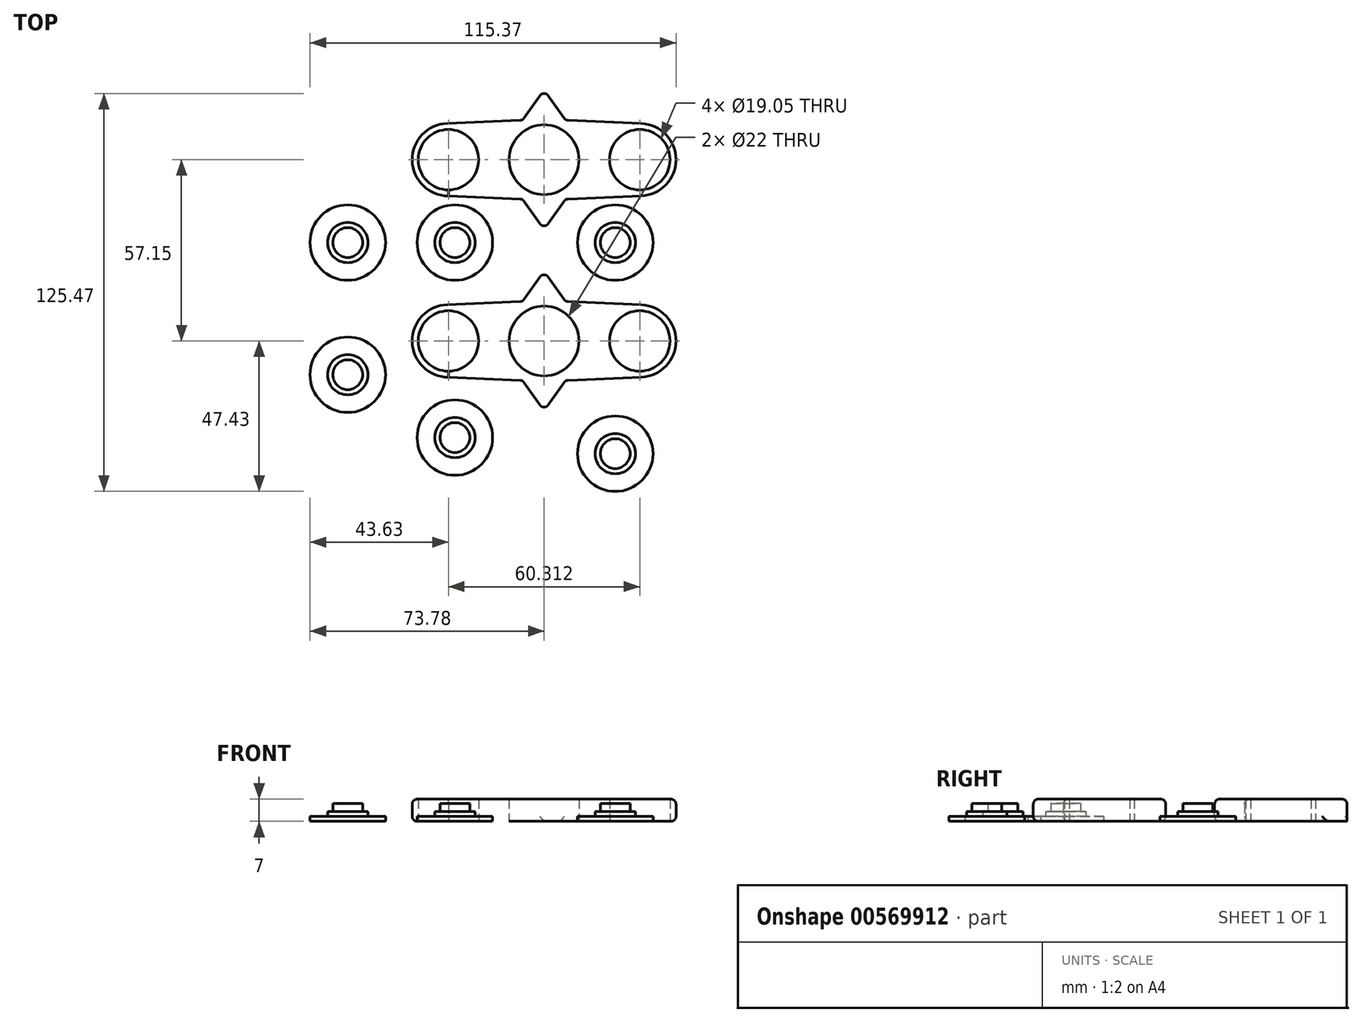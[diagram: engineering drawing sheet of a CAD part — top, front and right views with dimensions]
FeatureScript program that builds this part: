
annotation { "Feature Type Name" : "Feature", "Feature Type Description" : "" }
export const myFeature = defineFeature(function(context is Context, id is Id, definition is map)
    precondition{}
    {
        {
            var Q0;
            Q0=qCreatedBy(makeId("Top.planeOp"),FACE);
            var sketch = newSketch(context, id + "F0", { "sketchPlane" : qUnion([Q0])});
            skCircle(sketch, "E0", {"center": v(0, 0) * mm, "radius": 11 * mm});
            skCircle(sketch, "E1", {"center": v(-30.15, 0) * mm, "radius": 9.53 * mm});
            skCircle(sketch, "E2", {"center": v(30.16, 0) * mm, "radius": 9.53 * mm});
            skCircle(sketch, "E3", {"center": v(0, 0) * mm, "radius": 12.7 * mm});
            skCircle(sketch, "E4", {"center": v(30.16, 0) * mm, "radius": 11.43 * mm});
            skCircle(sketch, "E5", {"center": v(-30.15, 0) * mm, "radius": 11.43 * mm});
            skLineSegment(sketch, "E6", {"start": v(-30.15, -11.43) * mm, "end": v(0, -12.71) * mm});
            skLineSegment(sketch, "E7", {"start": v(0, -12.71) * mm, "end": v(30.64, -11.42) * mm});
            skLineSegment(sketch, "E8", {"start": v(-30.54, 11.42) * mm, "end": v(0, 12.71) * mm});
            skLineSegment(sketch, "E9", {"start": v(0, 12.71) * mm, "end": v(30.64, 11.42) * mm});
            skLineSegment(sketch, "E10", {"start": v(6.78, 12.43) * mm, "end": v(0, 22.06) * mm});
            skLineSegment(sketch, "E11", {"start": v(-6.76, 12.43) * mm, "end": v(0, 22.06) * mm});
            skLineSegment(sketch, "E12", {"start": v(0, -22.05) * mm, "end": v(6.76, -12.43) * mm});
            skLineSegment(sketch, "E13", {"start": v(0, -22.05) * mm, "end": v(-6.77, -12.42) * mm});
            skSolve(sketch);
        }
        {
            var Q0;
            Q0=makeQuery(id+"F0.imprint","IMPRINT",FACE,{"disambiguationData":[TD([[makeQuery(id+"F0.imprint","IMPRINT",EDGE,{"derivedFrom":sQuery(id+"F0.wireOp",EDGE,"E1")}),-1.0]])]});
            var Q1;
            Q1=makeQuery(id+"F0.imprint","IMPRINT",FACE,{"disambiguationData":[TD([[makeQuery(id+"F0.imprint","IMPRINT",EDGE,{"derivedFrom":sQuery(id+"F0.wireOp",EDGE,"E2")}),-1.0]])]});
            var Q2;
            {var subQ3=sQuery(id+"F0.wireOp",EDGE,"E12");Q2=makeQuery(id+"F0.imprint","IMPRINT",FACE,{"disambiguationData":[TD([[makeQuery(id+"F0.imprint","IMPRINT",EDGE,{"derivedFrom":subQ3}),1.0]])]});}
            var Q3;
            {var subQ0=sQuery(id+"F0.wireOp",EDGE,"E10");Q3=makeQuery(id+"F0.imprint","IMPRINT",FACE,{"disambiguationData":[TD([[makeQuery(id+"F0.imprint","IMPRINT",EDGE,{"derivedFrom":subQ0}),1.0]])]});}
            var Q4;
            Q4=makeQuery(id+"F0.imprint","IMPRINT",FACE,{"disambiguationData":[TD([[makeQuery(id+"F0.imprint","IMPRINT",EDGE,{"derivedFrom":sQuery(id+"F0.wireOp",EDGE,"E0")}),-1.0]])]});
            var Q5;
            {var subQ0=sQuery(id+"F0.wireOp",EDGE,"E6");var subQ2=sQuery(id+"F0.wireOp",EDGE,"E3");var subQ3=makeQuery(id+"F0.imprint","INTERSECT",VERTEX,{"derivedFrom":[subQ2,subQ0]});Q5=makeQuery(id+"F0.imprint","IMPRINT",FACE,{"disambiguationData":[TD([[makeQuery(id+"F0.imprint","IMPRINT",EDGE,{"disambiguationData":[TD([[subQ3,1.0]])],"derivedFrom":subQ2}),-1.0]])]});}
            var Q6;
            {var subQ1=sQuery(id+"F0.wireOp",EDGE,"E6");var subQ4=sQuery(id+"F0.wireOp",EDGE,"E3");var subQ5=makeQuery(id+"F0.imprint","INTERSECT",VERTEX,{"derivedFrom":[subQ4,subQ1]});Q6=makeQuery(id+"F0.imprint","IMPRINT",FACE,{"disambiguationData":[TD([[makeQuery(id+"F0.imprint","IMPRINT",EDGE,{"disambiguationData":[TD([[subQ5,-1.0]])],"derivedFrom":subQ4}),-1.0]])]});}
            extrude(context, id + "F1", {"entities" : qUnion([Q0, Q1, Q2, Q3, Q4, Q5, Q6]), "depth" : 7 * mm, "offsetDistance" : 25.4 * mm});
        }
        {
            var Q0;
            Q0=qCreatedBy(makeId("Top.planeOp"),FACE);
            var sketch = newSketch(context, id + "F2", { "sketchPlane" : qUnion([Q0])});
            skCircle(sketch, "E14", {"center": v(22.45, 31.02) * mm, "radius": 11.9 * mm});
            skSolve(sketch);
        }
        {
            var Q0;
            Q0=makeQuery(id+"F2.imprint","IMPRINT",FACE,{"disambiguationData":[TD([[makeQuery(id+"F2.imprint","IMPRINT",EDGE,{"derivedFrom":sQuery(id+"F2.wireOp",EDGE,"E14")}),1.0]])]});
            extrude(context, id + "F3", {"entities" : qUnion([Q0]), "depth" : 1.57 * mm, "offsetDistance" : 25.4 * mm});
        }
        {
            var Q0;
            Q0=makeQuery(id+"F3.opExtrude","CAP_FACE",FACE,{"disambiguationData":[OSD([sQuery(id+"F2.wireOp",EDGE,"E14")])],"isStart":false});
            var sketch = newSketch(context, id + "F4", { "sketchPlane" : qUnion([Q0])});
            skCircle(sketch, "E15", {"center": v(22.45, 31.02) * mm, "radius": 6.35 * mm});
            skSolve(sketch);
        }
        {
            var Q0;
            Q0=makeQuery(id+"F4.imprint","IMPRINT",FACE,{"disambiguationData":[TD([[makeQuery(id+"F4.imprint","IMPRINT",EDGE,{"derivedFrom":sQuery(id+"F4.wireOp",EDGE,"E15")}),1.0]])]});
            extrude(context, id + "F5", {"entities" : qUnion([Q0]), "operationType" : NewBodyOperationType.ADD, "depth" : 1.52 * mm, "offsetDistance" : 25.4 * mm});
        }
        {
            var Q0;
            Q0=makeQuery(id+"F5.opExtrude","CAP_FACE",FACE,{"disambiguationData":[OSD([sQuery(id+"F4.wireOp",EDGE,"E15")])],"isStart":false});
            var sketch = newSketch(context, id + "F6", { "sketchPlane" : qUnion([Q0])});
            skCircle(sketch, "E16", {"center": v(22.45, 31.02) * mm, "radius": 4.7 * mm});
            skSolve(sketch);
        }
        {
            var Q0;
            Q0=makeQuery(id+"F6.imprint","IMPRINT",FACE,{"disambiguationData":[TD([[makeQuery(id+"F6.imprint","IMPRINT",EDGE,{"derivedFrom":sQuery(id+"F6.wireOp",EDGE,"E16")}),1.0]])]});
            extrude(context, id + "F7", {"entities" : qUnion([Q0]), "operationType" : NewBodyOperationType.ADD, "depth" : 2.54 * mm, "offsetDistance" : 25.4 * mm});
        }
        {
            var Q0;
            Q0=makeQuery(id+"F3.opExtrude","SWEPT_BODY",BODY,{"disambiguationData":[OSD([sQuery(id+"F2.wireOp",EDGE,"E14")])]});
            transform(context, id + "F8", {"entities" : qUnion([Q0]), "transformType" : TransformType.TRANSLATION_3D, "dx" : -50.55 * mm, "dy" : 0 * mm, "dz" : 0 * mm, "makeCopy" : true});
        }
        {
            var Q0;
            Q0=makeQuery(id+"F8.opPattern","COPY",BODY,{"derivedFrom":makeQuery(id+"F3.opExtrude","SWEPT_BODY",BODY,{"disambiguationData":[OSD([sQuery(id+"F2.wireOp",EDGE,"E14")])]}),"instanceName":"1"});
            transform(context, id + "F9", {"entities" : qUnion([Q0]), "transformType" : TransformType.TRANSLATION_3D, "dx" : 0 * mm, "dy" : -61.47 * mm, "dz" : 0 * mm, "makeCopy" : true});
        }
        {
            var Q0;
            Q0=makeQuery(id+"F3.opExtrude","SWEPT_BODY",BODY,{"disambiguationData":[OSD([sQuery(id+"F2.wireOp",EDGE,"E14")])]});
            transform(context, id + "F10", {"entities" : qUnion([Q0]), "transformType" : TransformType.TRANSLATION_3D, "dx" : 0 * mm, "dy" : -66.55 * mm, "dz" : 0 * mm, "makeCopy" : true});
        }
        {
            var Q0;
            Q0=makeQuery(id+"F1.opExtrude","SWEPT_BODY",BODY,{"disambiguationData":[OSD([sQuery(id+"F0.wireOp",EDGE,"E0"),sQuery(id+"F0.wireOp",EDGE,"E1"),sQuery(id+"F0.wireOp",EDGE,"E2"),sQuery(id+"F0.wireOp",EDGE,"E4"),sQuery(id+"F0.wireOp",EDGE,"E5"),sQuery(id+"F0.wireOp",EDGE,"E6"),sQuery(id+"F0.wireOp",EDGE,"E7"),sQuery(id+"F0.wireOp",EDGE,"E8"),sQuery(id+"F0.wireOp",EDGE,"E9"),sQuery(id+"F0.wireOp",EDGE,"E10"),sQuery(id+"F0.wireOp",EDGE,"E11"),sQuery(id+"F0.wireOp",EDGE,"E12"),sQuery(id+"F0.wireOp",EDGE,"E13")])]});
            transform(context, id + "F11", {"entities" : qUnion([Q0]), "transformType" : TransformType.TRANSLATION_3D, "dx" : 0 * mm, "dy" : 57.15 * mm, "dz" : 0 * mm, "makeCopy" : true});
        }
        {
            var Q0;
            Q0=makeQuery(id+"F8.opPattern","COPY",BODY,{"derivedFrom":makeQuery(id+"F3.opExtrude","SWEPT_BODY",BODY,{"disambiguationData":[OSD([sQuery(id+"F2.wireOp",EDGE,"E14")])]}),"instanceName":"1"});
            transform(context, id + "F12", {"entities" : qUnion([Q0]), "transformType" : TransformType.TRANSLATION_3D, "dx" : -33.78 * mm, "dy" : 0 * mm, "dz" : 0 * mm, "makeCopy" : true});
        }
        {
            var Q0;
            Q0=makeQuery(id+"F12.opPattern","COPY",BODY,{"derivedFrom":makeQuery(id+"F8.opPattern","COPY",BODY,{"derivedFrom":makeQuery(id+"F3.opExtrude","SWEPT_BODY",BODY,{"disambiguationData":[OSD([sQuery(id+"F2.wireOp",EDGE,"E14")])]}),"instanceName":"1"}),"instanceName":"1"});
            transform(context, id + "F13", {"entities" : qUnion([Q0]), "transformType" : TransformType.TRANSLATION_3D, "dx" : 0 * mm, "dy" : -41.66 * mm, "dz" : 0 * mm, "makeCopy" : true});
        }
        {
            var Q0;
            Q0=makeQuery(id+"F1.opExtrude","CAP_EDGE",EDGE,{"disambiguationData":[OSD([sQuery(id+"F0.wireOp",EDGE,"E6")])],"isStart":false});
            var Q1;
            Q1=makeQuery(id+"F1.opExtrude","CAP_EDGE",EDGE,{"disambiguationData":[OSD([sQuery(id+"F0.wireOp",EDGE,"E5")])],"isStart":false});
            var Q2;
            Q2=makeQuery(id+"F1.opExtrude","CAP_EDGE",EDGE,{"disambiguationData":[OSD([sQuery(id+"F0.wireOp",EDGE,"E9")])],"isStart":false});
            var Q3;
            Q3=makeQuery(id+"F1.opExtrude","CAP_EDGE",EDGE,{"disambiguationData":[OSD([sQuery(id+"F0.wireOp",EDGE,"E10")])],"isStart":false});
            var Q4;
            Q4=makeQuery(id+"F1.opExtrude","CAP_EDGE",EDGE,{"disambiguationData":[OSD([sQuery(id+"F0.wireOp",EDGE,"E11")])],"isStart":false});
            var Q5;
            Q5=makeQuery(id+"F1.opExtrude","CAP_EDGE",EDGE,{"disambiguationData":[OSD([sQuery(id+"F0.wireOp",EDGE,"E13")])],"isStart":false});
            var Q6;
            Q6=makeQuery(id+"F1.opExtrude","CAP_EDGE",EDGE,{"disambiguationData":[OSD([sQuery(id+"F0.wireOp",EDGE,"E12")])],"isStart":false});
            var Q7;
            Q7=makeQuery(id+"F11.opPattern","COPY",EDGE,{"derivedFrom":makeQuery(id+"F1.opExtrude","CAP_EDGE",EDGE,{"disambiguationData":[OSD([sQuery(id+"F0.wireOp",EDGE,"E12")])],"isStart":false}),"instanceName":"1"});
            var Q8;
            Q8=makeQuery(id+"F11.opPattern","COPY",EDGE,{"derivedFrom":makeQuery(id+"F1.opExtrude","CAP_EDGE",EDGE,{"disambiguationData":[OSD([sQuery(id+"F0.wireOp",EDGE,"E13")])],"isStart":false}),"instanceName":"1"});
            var Q9;
            Q9=makeQuery(id+"F11.opPattern","COPY",EDGE,{"derivedFrom":makeQuery(id+"F1.opExtrude","CAP_EDGE",EDGE,{"disambiguationData":[OSD([sQuery(id+"F0.wireOp",EDGE,"E6")])],"isStart":false}),"instanceName":"1"});
            var Q10;
            Q10=makeQuery(id+"F11.opPattern","COPY",EDGE,{"derivedFrom":makeQuery(id+"F1.opExtrude","CAP_EDGE",EDGE,{"disambiguationData":[OSD([sQuery(id+"F0.wireOp",EDGE,"E7")])],"isStart":false}),"instanceName":"1"});
            var Q11;
            Q11=makeQuery(id+"F11.opPattern","COPY",EDGE,{"derivedFrom":makeQuery(id+"F1.opExtrude","CAP_EDGE",EDGE,{"disambiguationData":[OSD([sQuery(id+"F0.wireOp",EDGE,"E4")])],"isStart":false}),"instanceName":"1"});
            var Q12;
            Q12=makeQuery(id+"F11.opPattern","COPY",EDGE,{"derivedFrom":makeQuery(id+"F1.opExtrude","CAP_EDGE",EDGE,{"disambiguationData":[OSD([sQuery(id+"F0.wireOp",EDGE,"E10")])],"isStart":false}),"instanceName":"1"});
            var Q13;
            Q13=makeQuery(id+"F11.opPattern","COPY",EDGE,{"derivedFrom":makeQuery(id+"F1.opExtrude","CAP_EDGE",EDGE,{"disambiguationData":[OSD([sQuery(id+"F0.wireOp",EDGE,"E8")])],"isStart":false}),"instanceName":"1"});
            var Q14;
            Q14=makeQuery(id+"F11.opPattern","COPY",EDGE,{"derivedFrom":makeQuery(id+"F1.opExtrude","CAP_EDGE",EDGE,{"disambiguationData":[OSD([sQuery(id+"F0.wireOp",EDGE,"E11")])],"isStart":false}),"instanceName":"1"});
            var Q15;
            Q15=makeQuery(id+"F11.opPattern","COPY",EDGE,{"derivedFrom":makeQuery(id+"F1.opExtrude","CAP_EDGE",EDGE,{"disambiguationData":[OSD([sQuery(id+"F0.wireOp",EDGE,"E5")])],"isStart":false}),"instanceName":"1"});
            var Q16;
            Q16=makeQuery(id+"F11.opPattern","COPY",EDGE,{"derivedFrom":makeQuery(id+"F1.opExtrude","CAP_EDGE",EDGE,{"disambiguationData":[OSD([sQuery(id+"F0.wireOp",EDGE,"E9")])],"isStart":true}),"instanceName":"1"});
            var Q17;
            Q17=makeQuery(id+"F11.opPattern","COPY",EDGE,{"derivedFrom":makeQuery(id+"F1.opExtrude","CAP_EDGE",EDGE,{"disambiguationData":[OSD([sQuery(id+"F0.wireOp",EDGE,"E11")])],"isStart":true}),"instanceName":"1"});
            var Q18;
            Q18=makeQuery(id+"F11.opPattern","COPY",EDGE,{"derivedFrom":makeQuery(id+"F1.opExtrude","CAP_EDGE",EDGE,{"disambiguationData":[OSD([sQuery(id+"F0.wireOp",EDGE,"E8")])],"isStart":true}),"instanceName":"1"});
            var Q19;
            Q19=makeQuery(id+"F11.opPattern","COPY",EDGE,{"derivedFrom":makeQuery(id+"F1.opExtrude","CAP_EDGE",EDGE,{"disambiguationData":[OSD([sQuery(id+"F0.wireOp",EDGE,"E6")])],"isStart":true}),"instanceName":"1"});
            var Q20;
            Q20=makeQuery(id+"F11.opPattern","COPY",EDGE,{"derivedFrom":makeQuery(id+"F1.opExtrude","CAP_EDGE",EDGE,{"disambiguationData":[OSD([sQuery(id+"F0.wireOp",EDGE,"E5")])],"isStart":true}),"instanceName":"1"});
            var Q21;
            Q21=makeQuery(id+"F11.opPattern","COPY",EDGE,{"derivedFrom":makeQuery(id+"F1.opExtrude","CAP_EDGE",EDGE,{"disambiguationData":[OSD([sQuery(id+"F0.wireOp",EDGE,"E12")])],"isStart":true}),"instanceName":"1"});
            var Q22;
            Q22=makeQuery(id+"F11.opPattern","COPY",EDGE,{"derivedFrom":makeQuery(id+"F1.opExtrude","CAP_EDGE",EDGE,{"disambiguationData":[OSD([sQuery(id+"F0.wireOp",EDGE,"E13")])],"isStart":true}),"instanceName":"1"});
            var Q23;
            Q23=makeQuery(id+"F1.opExtrude","CAP_EDGE",EDGE,{"disambiguationData":[OSD([sQuery(id+"F0.wireOp",EDGE,"E8")])],"isStart":true});
            var Q24;
            Q24=makeQuery(id+"F1.opExtrude","CAP_EDGE",EDGE,{"disambiguationData":[OSD([sQuery(id+"F0.wireOp",EDGE,"E7")])],"isStart":true});
            var Q25;
            Q25=makeQuery(id+"F1.opExtrude","CAP_EDGE",EDGE,{"disambiguationData":[OSD([sQuery(id+"F0.wireOp",EDGE,"E12")])],"isStart":true});
            var Q26;
            Q26=makeQuery(id+"F1.opExtrude","CAP_EDGE",EDGE,{"disambiguationData":[OSD([sQuery(id+"F0.wireOp",EDGE,"E6")])],"isStart":true});
            var Q27;
            Q27=makeQuery(id+"F1.opExtrude","CAP_EDGE",EDGE,{"disambiguationData":[OSD([sQuery(id+"F0.wireOp",EDGE,"E13")])],"isStart":true});
            var Q28;
            Q28=makeQuery(id+"F1.opExtrude","CAP_EDGE",EDGE,{"disambiguationData":[OSD([sQuery(id+"F0.wireOp",EDGE,"E11")])],"isStart":true});
            var Q29;
            Q29=makeQuery(id+"F1.opExtrude","CAP_EDGE",EDGE,{"disambiguationData":[OSD([sQuery(id+"F0.wireOp",EDGE,"E10")])],"isStart":true});
            var Q30;
            Q30=makeQuery(id+"F1.opExtrude","CAP_EDGE",EDGE,{"disambiguationData":[OSD([sQuery(id+"F0.wireOp",EDGE,"E5")])],"isStart":true});
            var Q31;
            Q31=makeQuery(id+"F11.opPattern","COPY",EDGE,{"derivedFrom":makeQuery(id+"F1.opExtrude","SWEPT_EDGE",EDGE,{"disambiguationData":[OSD([sQuery(id+"F0.wireOp",EDGE,"E10"),sQuery(id+"F0.wireOp",EDGE,"E11")])]}),"instanceName":"1"});
            var Q32;
            Q32=makeQuery(id+"F11.opPattern","COPY",EDGE,{"derivedFrom":makeQuery(id+"F1.opExtrude","SWEPT_EDGE",EDGE,{"disambiguationData":[OSD([sQuery(id+"F0.wireOp",EDGE,"E8"),sQuery(id+"F0.wireOp",EDGE,"E11")])]}),"instanceName":"1"});
            var Q33;
            Q33=makeQuery(id+"F11.opPattern","COPY",EDGE,{"derivedFrom":makeQuery(id+"F1.opExtrude","SWEPT_EDGE",EDGE,{"disambiguationData":[OSD([sQuery(id+"F0.wireOp",EDGE,"E9"),sQuery(id+"F0.wireOp",EDGE,"E10")])]}),"instanceName":"1"});
            var Q34;
            Q34=makeQuery(id+"F1.opExtrude","SWEPT_EDGE",EDGE,{"disambiguationData":[OSD([sQuery(id+"F0.wireOp",EDGE,"E8"),sQuery(id+"F0.wireOp",EDGE,"E11")])]});
            var Q35;
            Q35=makeQuery(id+"F1.opExtrude","SWEPT_EDGE",EDGE,{"disambiguationData":[OSD([sQuery(id+"F0.wireOp",EDGE,"E10"),sQuery(id+"F0.wireOp",EDGE,"E11")])]});
            var Q36;
            Q36=makeQuery(id+"F1.opExtrude","SWEPT_EDGE",EDGE,{"disambiguationData":[OSD([sQuery(id+"F0.wireOp",EDGE,"E9"),sQuery(id+"F0.wireOp",EDGE,"E10")])]});
            var Q37;
            Q37=makeQuery(id+"F11.opPattern","COPY",EDGE,{"derivedFrom":makeQuery(id+"F1.opExtrude","SWEPT_EDGE",EDGE,{"disambiguationData":[OSD([sQuery(id+"F0.wireOp",EDGE,"E6"),sQuery(id+"F0.wireOp",EDGE,"E13")])]}),"instanceName":"1"});
            var Q38;
            Q38=makeQuery(id+"F11.opPattern","COPY",EDGE,{"derivedFrom":makeQuery(id+"F1.opExtrude","SWEPT_EDGE",EDGE,{"disambiguationData":[OSD([sQuery(id+"F0.wireOp",EDGE,"E12"),sQuery(id+"F0.wireOp",EDGE,"E13")])]}),"instanceName":"1"});
            var Q39;
            Q39=makeQuery(id+"F11.opPattern","COPY",EDGE,{"derivedFrom":makeQuery(id+"F1.opExtrude","SWEPT_EDGE",EDGE,{"disambiguationData":[OSD([sQuery(id+"F0.wireOp",EDGE,"E7"),sQuery(id+"F0.wireOp",EDGE,"E12")])]}),"instanceName":"1"});
            var Q40;
            Q40=makeQuery(id+"F1.opExtrude","SWEPT_EDGE",EDGE,{"disambiguationData":[OSD([sQuery(id+"F0.wireOp",EDGE,"E6"),sQuery(id+"F0.wireOp",EDGE,"E13")])]});
            var Q41;
            Q41=makeQuery(id+"F1.opExtrude","SWEPT_EDGE",EDGE,{"disambiguationData":[OSD([sQuery(id+"F0.wireOp",EDGE,"E7"),sQuery(id+"F0.wireOp",EDGE,"E12")])]});
            var Q42;
            Q42=makeQuery(id+"F1.opExtrude","SWEPT_FACE",FACE,{"disambiguationData":[OSD([sQuery(id+"F0.wireOp",EDGE,"E13")])]});
            fillet(context, id + "F14", {"entities" : qUnion([Q0, Q1, Q2, Q3, Q4, Q5, Q6, Q7, Q8, Q9, Q10, Q11, Q12, Q13, Q14, Q15, Q16, Q17, Q18, Q19, Q20, Q21, Q22, Q23, Q24, Q25, Q26, Q27, Q28, Q29, Q30, Q31, Q32, Q33, Q34, Q35, Q36, Q37, Q38, Q39, Q40, Q41, Q42]), "radius" : 1.59 * mm, "tangentPropagation" : true, "allowEdgeOverflow" : false});
        }
    });
